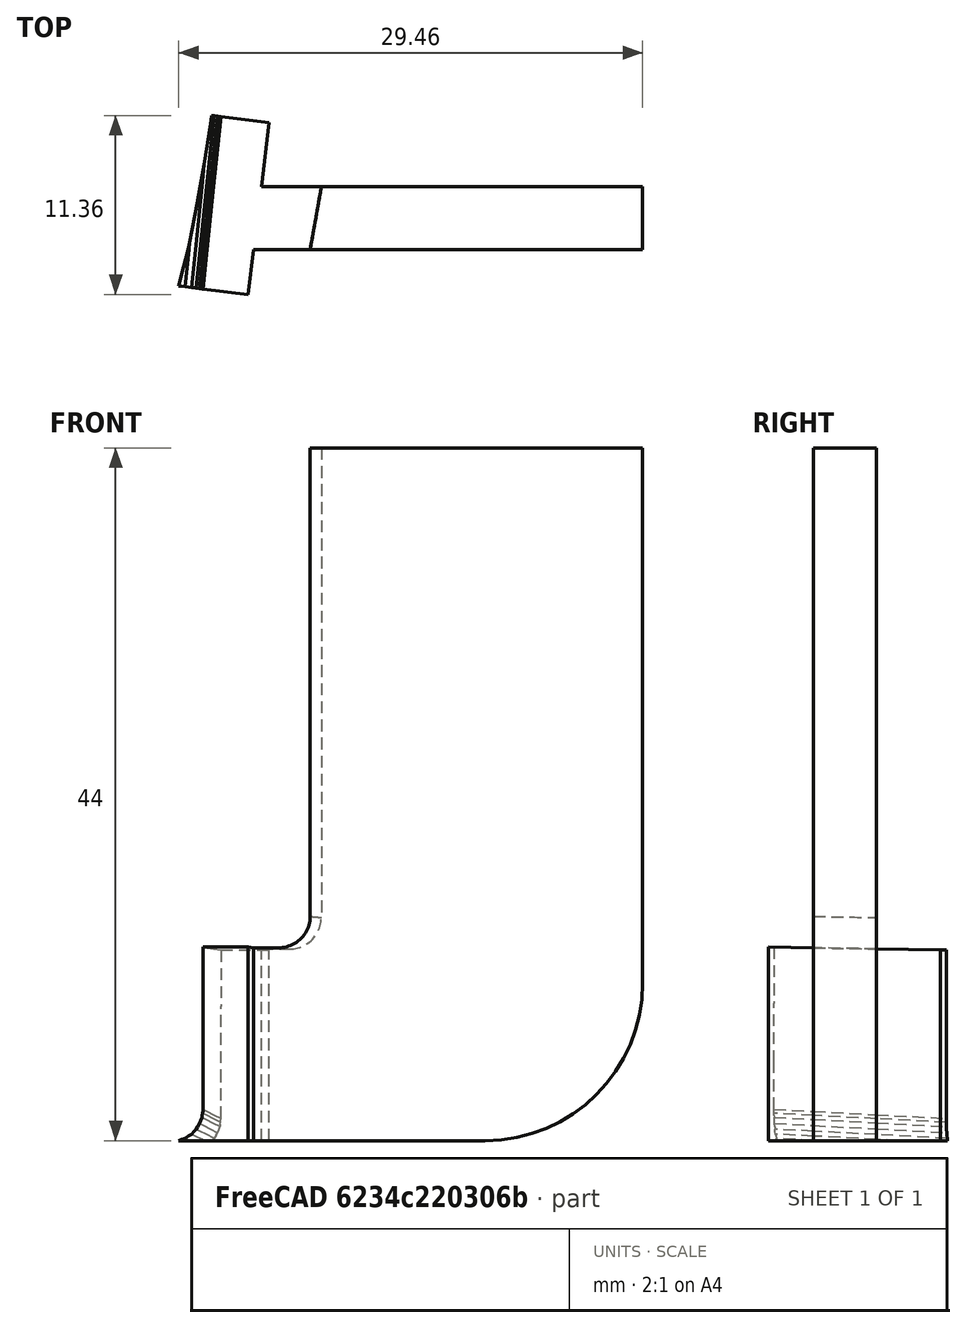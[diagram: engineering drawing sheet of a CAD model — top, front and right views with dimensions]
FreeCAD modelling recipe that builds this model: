
FCSTD DOCUMENT  (FreeCAD 0.16R6704 (Git))
Label: right-bracket
License: All rights reserved
LicenseURL: http://en.wikipedia.org/wiki/All_rights_reserved
objects: Part::Feature×2, Part::MultiFuse×1, Part::Fillet×1, Part::Box×1, Part::Cut×1
note: 6 computed .brp shape members not serialized (recipe doc carries the construction recipe); baked Part::Feature solids carry a one-line shape summary decoded from their .brp

FEATURE [Part::Feature] Solid001
  shape: bbox 32.6 x 97.32 x 103 mm, 24 faces (baked)
FEATURE [Part::Feature] Solid003
  shape: bbox 5.752 x 11.37 x 12.3 mm, 22 faces (baked)
FEATURE [Part::MultiFuse] Fusion002
  Shapes = -> [Solid003,Solid001]
FEATURE [Part::Fillet] Fillet009
  Base = -> Fusion002
  Edges = 1 edges r=10: [Edge110]
  Placement = pos=(0,90.5,-451) rot=(0,0,1;0rad)
FEATURE [Part::Box] Box  label="Cube"
  Height = 67
  Length = 28
  Placement = pos=(-13,-6,44) rot=(0,0,1;0rad)
  Width = 13
FEATURE [Part::Cut] Cut  label="Right-Bracket"
  Base = -> Fillet009
  Tool = -> Box
